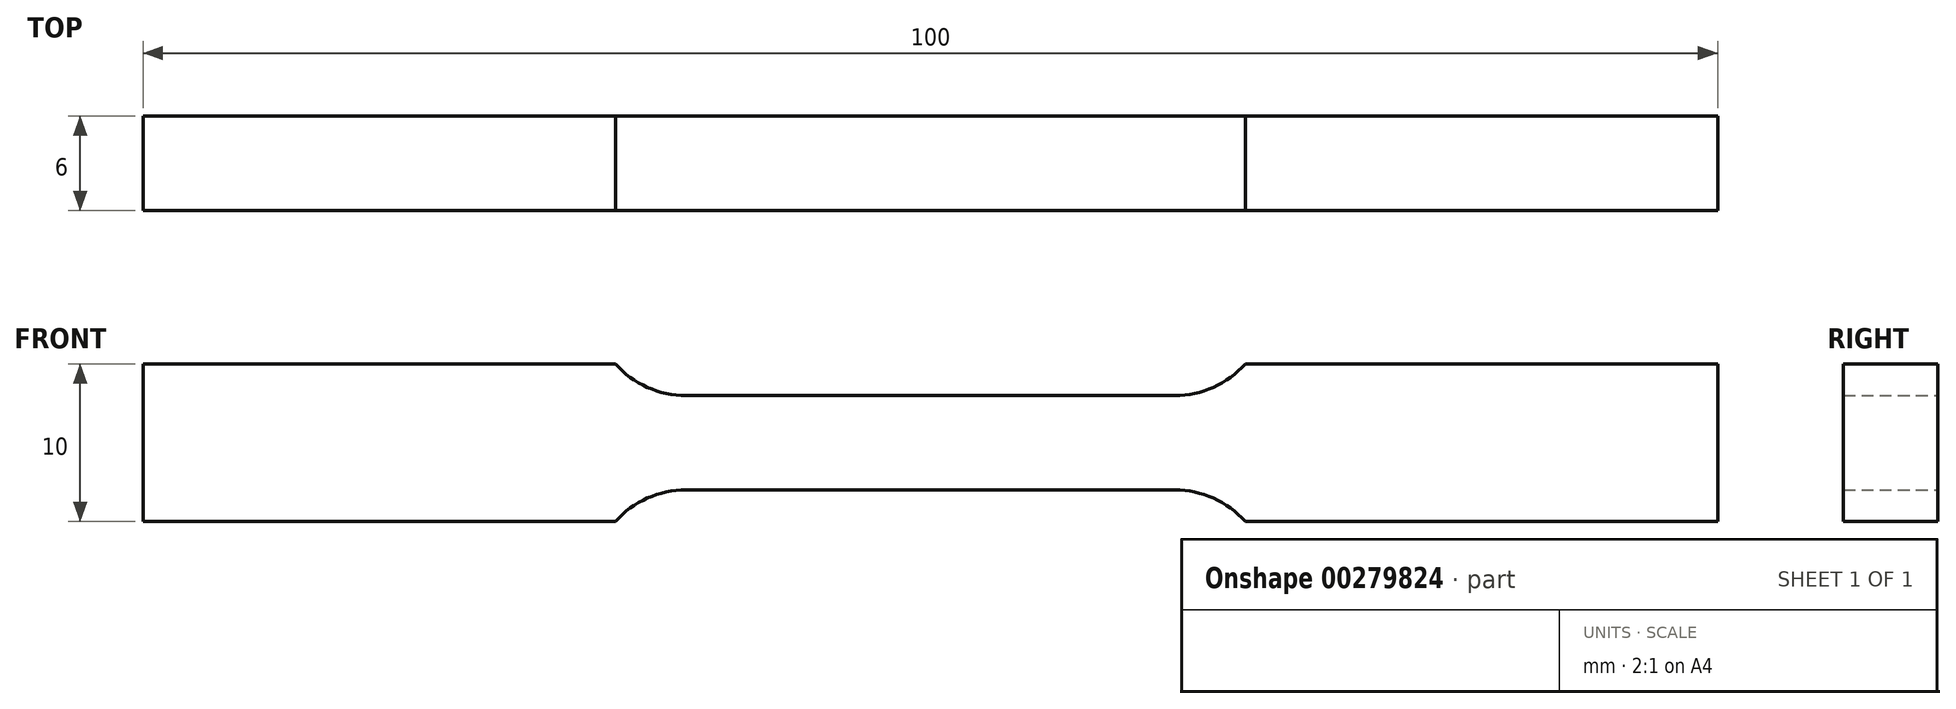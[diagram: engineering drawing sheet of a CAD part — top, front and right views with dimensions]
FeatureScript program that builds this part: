
annotation { "Feature Type Name" : "Feature", "Feature Type Description" : "" }
export const myFeature = defineFeature(function(context is Context, id is Id, definition is map)
    precondition{}
    {
        {
            var Q0;
            Q0=qCreatedBy(makeId("Front.planeOp"),FACE);
            var sketch = newSketch(context, id + "F0", { "sketchPlane" : qUnion([Q0])});
            skLineSegment(sketch, "E0", {"start": v(0, 3) * mm, "end": v(15.53, 3) * mm});
            skArc(sketch, "E1", {"start": v(15.53, 3) * mm, "mid": v(17.98, 3.52) * mm, "end": v(20, 5) * mm});
            skLineSegment(sketch, "E2", {"start": v(20, 5) * mm, "end": v(50, 5) * mm});
            skLineSegment(sketch, "E3", {"start": v(50, 5) * mm, "end": v(50, 0) * mm});
            skLineSegment(sketch, "E4.MirrorCS", {"start": v(0, -3) * mm, "end": v(15.53, -3) * mm});
            skLineSegment(sketch, "E5.MirrorCS", {"start": v(50, -5) * mm, "end": v(50, 0) * mm});
            skLineSegment(sketch, "E6.MirrorCS", {"start": v(20, -5) * mm, "end": v(50, -5) * mm});
            skArc(sketch, "E7.MirrorCS", {"start": v(15.53, -3) * mm, "mid": v(17.98, -3.52) * mm, "end": v(20, -5) * mm});
            skArc(sketch, "E8.MirrorCS", {"start": v(-15.53, -3) * mm, "mid": v(-17.98, -3.52) * mm, "end": v(-20, -5) * mm});
            skLineSegment(sketch, "E9.MirrorCS", {"start": v(-20, -5) * mm, "end": v(-50, -5) * mm});
            skArc(sketch, "E10.MirrorCS", {"start": v(-15.53, 3) * mm, "mid": v(-17.98, 3.52) * mm, "end": v(-20, 5) * mm});
            skLineSegment(sketch, "E11.MirrorCS", {"start": v(-20, 5) * mm, "end": v(-50, 5) * mm});
            skLineSegment(sketch, "E12.MirrorCS", {"start": v(-50, -5) * mm, "end": v(-50, 0) * mm});
            skLineSegment(sketch, "E13.MirrorCS", {"start": v(0, 3) * mm, "end": v(-15.53, 3) * mm});
            skLineSegment(sketch, "E14.MirrorCS", {"start": v(-50, 5) * mm, "end": v(-50, 0) * mm});
            skLineSegment(sketch, "E15.MirrorCS", {"start": v(0, -3) * mm, "end": v(-15.53, -3) * mm});
            skSolve(sketch);
        }
        {
            var Q0;
            Q0=makeQuery(id+"F0.imprint","IMPRINT",FACE,{"disambiguationData":[TD([[makeQuery(id+"F0.imprint","IMPRINT",EDGE,{"derivedFrom":sQuery(id+"F0.wireOp",EDGE,"E0")}),-1.0]])]});
            extrude(context, id + "F1", {"entities" : qUnion([Q0]), "endBound" : BoundingType.SYMMETRIC, "depth" : 6 * mm});
        }
    });
